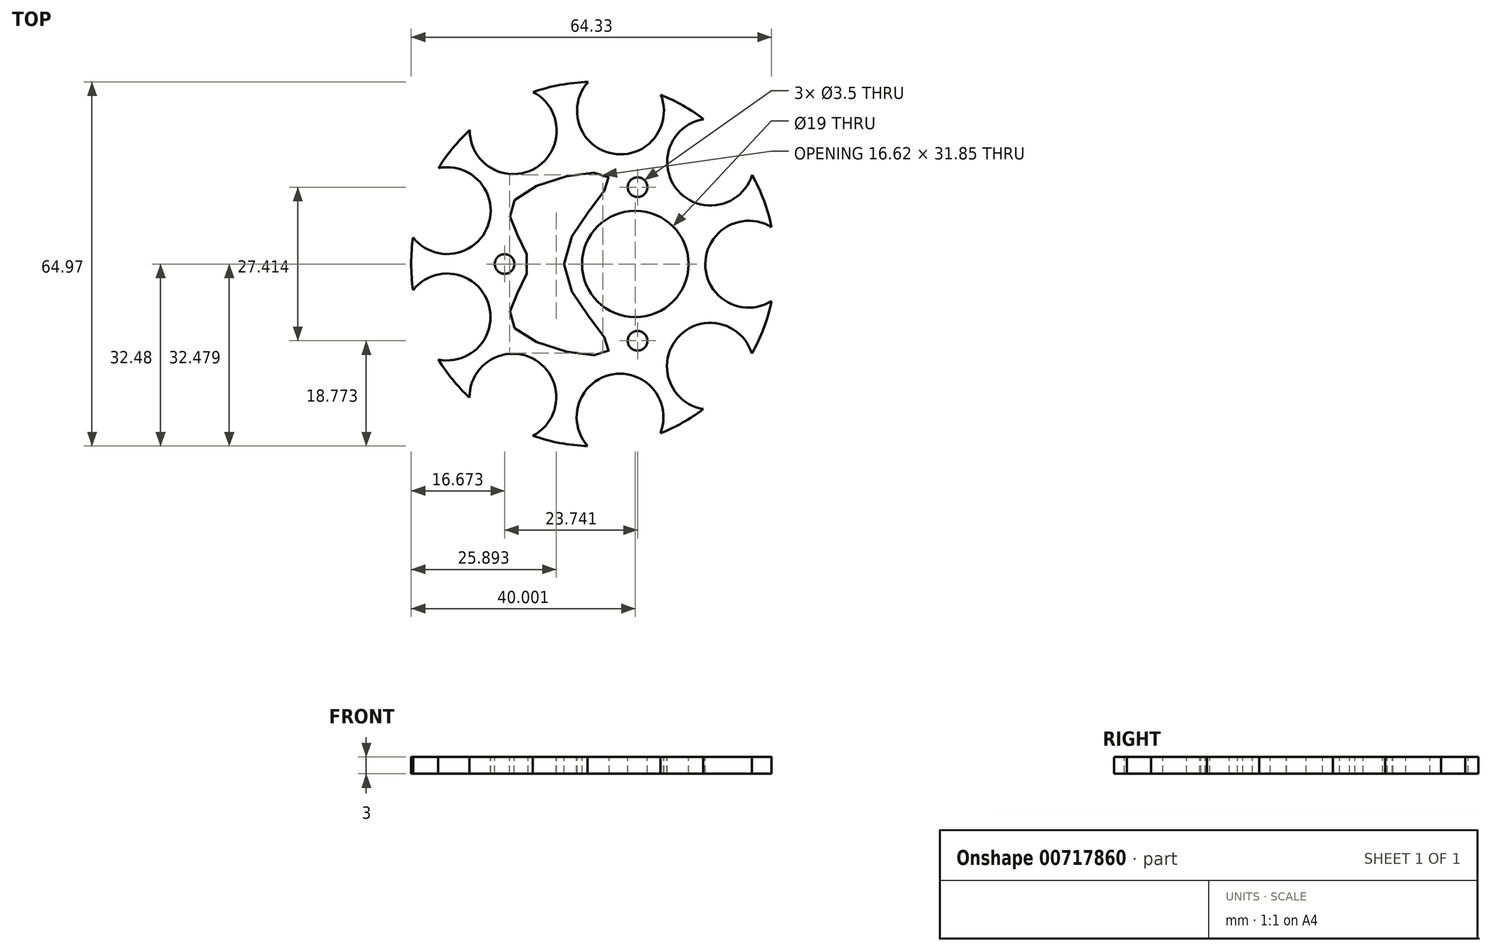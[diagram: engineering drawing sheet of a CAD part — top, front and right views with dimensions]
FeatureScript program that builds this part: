
annotation { "Feature Type Name" : "Feature", "Feature Type Description" : "" }
export const myFeature = defineFeature(function(context is Context, id is Id, definition is map)
    precondition{}
    {
        {
            var Q0;
            Q0=qCreatedBy(makeId("Top.planeOp"),FACE);
            var sketch = newSketch(context, id + "F0", { "sketchPlane" : qUnion([Q0])});
            skCircle(sketch, "E0", {"center": v(0.03, 0) * mm, "radius": 32.5 * mm});
            skCircle(sketch, "E1", {"center": v(27.78, -0.04) * mm, "radius": 7.75 * mm});
            skCircle(sketch, "E2.1.0", {"center": v(20.98, 18.2) * mm, "radius": 7.75 * mm});
            skCircle(sketch, "E2.2.0", {"center": v(4.88, 27.32) * mm, "radius": 7.75 * mm});
            skCircle(sketch, "E2.3.0", {"center": v(-14.26, 23.8) * mm, "radius": 7.75 * mm});
            skCircle(sketch, "E2.4.0", {"center": v(-26.03, 9.52) * mm, "radius": 7.75 * mm});
            skCircle(sketch, "E2.5.0", {"center": v(-26.06, -9.46) * mm, "radius": 7.75 * mm});
            skCircle(sketch, "E2.6.0", {"center": v(-14.32, -23.75) * mm, "radius": 7.75 * mm});
            skCircle(sketch, "E2.7.0", {"center": v(4.81, -27.33) * mm, "radius": 7.75 * mm});
            skCircle(sketch, "E2.8.0", {"center": v(20.93, -18.25) * mm, "radius": 7.75 * mm});
            skCircle(sketch, "E3", {"center": v(7.53, 0) * mm, "radius": 9.5 * mm});
            skCircle(sketch, "E4", {"center": v(-15.8, 0) * mm, "radius": 1.75 * mm});
            skCircle(sketch, "E5.1.0", {"center": v(7.94, -13.7) * mm, "radius": 1.75 * mm});
            skCircle(sketch, "E5.2.0", {"center": v(7.94, 13.7) * mm, "radius": 1.75 * mm});
            skPoint(sketch, "E6", {"position": v(2.67, 15.6) * mm});
            skPoint(sketch, "E7.MirrorP", {"position": v(2.67, -15.6) * mm});
            skPoint(sketch, "E8", {"position": v(-5.16, 0) * mm});
            skPoint(sketch, "E9", {"position": v(-11.57, 0) * mm});
            skPoint(sketch, "E10", {"position": v(-14.47, 10.8) * mm});
            skPoint(sketch, "E11.MirrorP", {"position": v(-14.47, -10.8) * mm});
            skFitSpline(sketch, "E12", {"points": [v(-5.16, 0) * mm, v(2.67, 15.6) * mm, v(-14.47, 10.8) * mm, v(-11.57, 0) * mm, v(-14.47, -10.8) * mm, v(2.67, -15.6) * mm, v(-5.16, 0) * mm]});
            skSolve(sketch);
        }
        {
            var Q0;
            Q0=makeQuery(id+"F0.imprint","IMPRINT",FACE,{"disambiguationData":[TD([[makeQuery(id+"F0.imprint","IMPRINT",EDGE,{"derivedFrom":sQuery(id+"F0.wireOp",EDGE,"E3")}),-1.0]])]});
            extrude(context, id + "F1", {"entities" : qUnion([Q0]), "oppositeDirection" : true, "depth" : 3 * mm, "offsetDistance" : 25 * mm});
        }
    });
